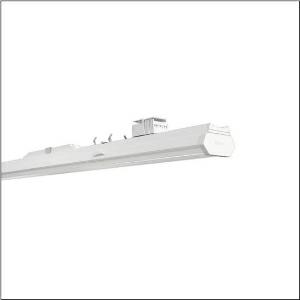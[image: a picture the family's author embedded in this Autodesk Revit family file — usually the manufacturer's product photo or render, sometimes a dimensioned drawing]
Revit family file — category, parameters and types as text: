
# Revit family: licross_r__21_protected_ho_52tp12dn4e5md_2ebe
name_source: partatom
category: Lighting Fixtures
units: mm (PartAtom-declared; Revit-internal decimal feet)

## family parameters
Cut with Voids When Loaded = No
Host = Face
Light Source = No
Part Type = Normal
Room Calculation Point = No
Round Connector Dimension = Use Diameter
Shared = No

## types (1)
- --- (1 x LED, 2200 lm, 14.2 W, 4000K)
    Apparent Load = 14 VA
    CIE Flux Codes = 70 91 97 98 100
    Color Rendering = 80
    Color Temperature = 4000K
    Default Elevation = 1800 mm
    Description = Licross® 21 Protected HO, luminaire insert, of sheet steel, galvanised, coil coated, white, length: 1.500mm, width: 90mm, height: 103mm, LED rated luminous flux: 14.690lm, light colour: 840, control gear: DALI 2 (for two DALI lines), with plug, 6-pole, with phase selection, mains connection: 220..240V, AC/DC, 0/50..60Hz, rated input power: 85W, without changeover relay, for emergency light function, for central battery installations according to DIN EN 60598-2-22, internal wiring halogen-free, primary light control with lens, of plastic, primary optical cover: cover, of PMMA, light emission: direct distribution, primary light characteristic: symmetric, protection rating (complete): IP64, insulation class (complete): insulation class I (protective earthing), certification: CE, ENEC, VDE, UKCA, protection symbol: D if used in an environment with conductive dust loads with corresponding accessories, impact resistance: IK06, permissible ambient temperature for indoor applications: -25..+35°C, standard: EN 60598-2-22, corresponds to IFS (International Featured Standards) requirements for safety and quality in the food industry, reducing of maximum allowable ambient temperature of 5°C with ceiling mounting, LABS conformity tested according to VDMA 24364:2018-05, packaging unit: 1 piece
    Height = 92 mm
    Lamp = 1 x LED
    Lamp Light Flux = 2200 lm
    Lamp Power = 14.2 W
    Lamp count = 1
    Length = 1500 mm
    Luminous efficacy = 155 lm/W
    Manufacturer = Siteco
    ModVariant = No
    Model = 52TP12DN4E5MD
    Mounting Place = Ceiling
    Mounting Type = Pendant
    Number of Poles = 1
    OnlyDefault = Yes
    Power Factor = 1
    Product Name = Licross® 21 Protected HO
    Product group = luminaire insert | ceiling pendant
    ProductGroupID = 902
    Protection Class = Protection class I
    Protection Degree = IP 64
    RLX_Detail_Level = 1
    RLX_Emergency_Light_Flux = 0 lm
    RLX_Emergency_Type = 0
    RLX_Emergency_Type_DB = No
    RlxData = <blob elided: 24901 chars, md5=ef4a5b15>
    Socket = socket
    Standby Power = 0 W
    System Light Flux = 2200 lm
    System Power = 14 W
    Type Comments = : DC mode (central or group accumulator) initial emergency light level
    Type Image = l_1256148.jpg
    URL = http://relux.com
    VarID = @adj_137867
    Voltage = 0 V
    Weight = 0.00 kg
    Width = 88 mm

## geometry (parser evidence)
native form markers: Blend x4, Sweep x11
no freeform markers — native parametric forms only
